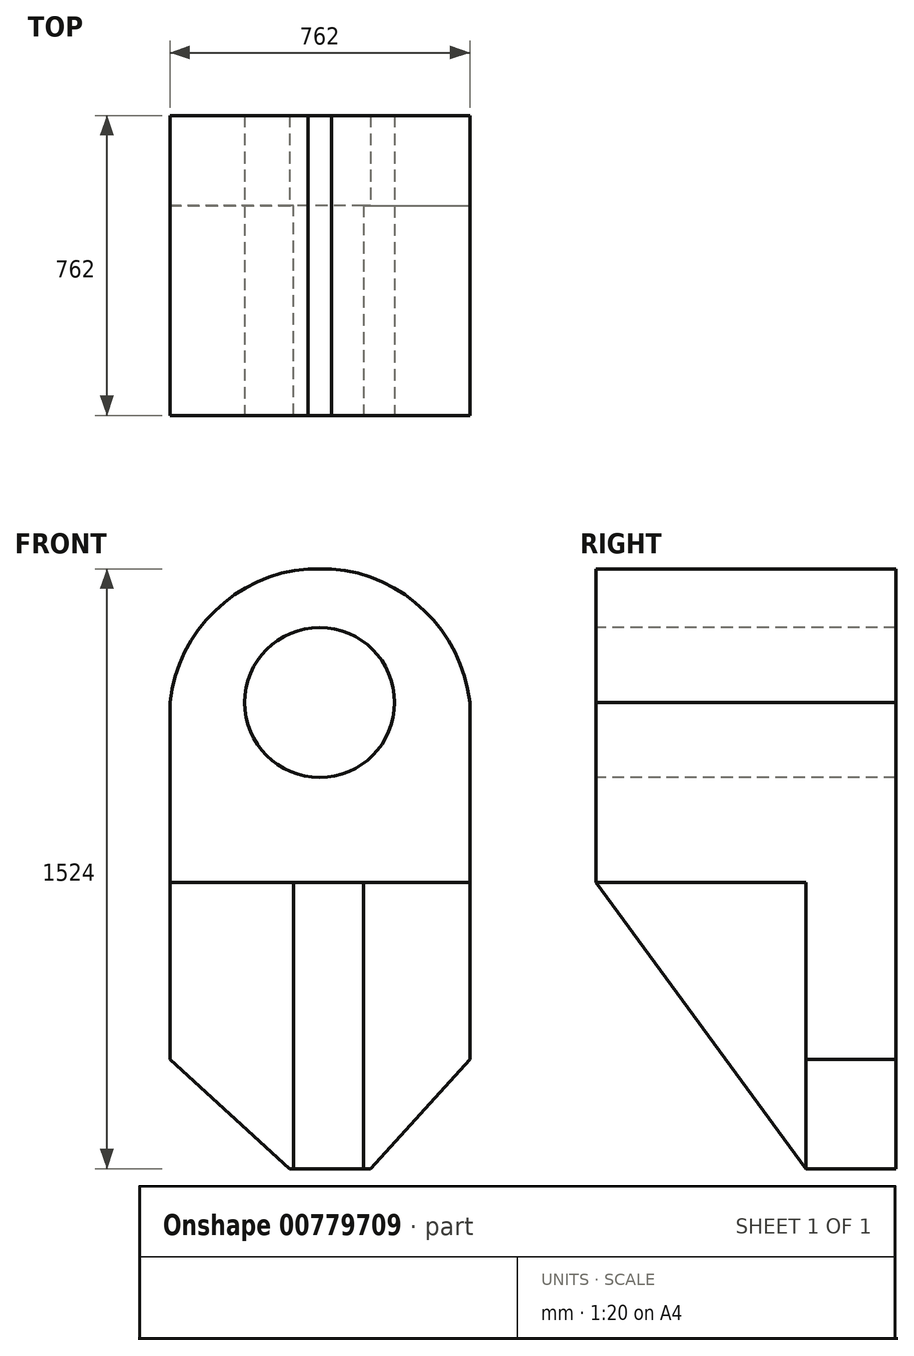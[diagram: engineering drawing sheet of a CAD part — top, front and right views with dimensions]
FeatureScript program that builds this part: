
annotation { "Feature Type Name" : "Feature", "Feature Type Description" : "" }
export const myFeature = defineFeature(function(context is Context, id is Id, definition is map)
    precondition{}
    {
        {
            var Q0;
            Q0=qCreatedBy(makeId("Front.planeOp"),FACE);
            var sketch = newSketch(context, id + "F0", { "sketchPlane" : qUnion([Q0])});
            skLineSegment(sketch, "E0", {"start": v(0, 0) * mm, "end": v(762, 0) * mm});
            skLineSegment(sketch, "E1", {"start": v(762, 0) * mm, "end": v(762, -1524) * mm});
            skLineSegment(sketch, "E2", {"start": v(762, -1524) * mm, "end": v(0, -1524) * mm});
            skLineSegment(sketch, "E3", {"start": v(0, -1524) * mm, "end": v(0, 0) * mm});
            skSolve(sketch);
        }
        {
            var Q0;
            Q0 = qSketchRegion(id + "F0", true);
            extrude(context, id + "F1", {"entities" : qUnion([Q0]), "depth" : 762 * mm, "offsetDistance" : 25.4 * mm});
        }
        {
            var Q0;
            Q0=makeQuery(id+"F1.opExtrude","CAP_FACE",FACE,{"disambiguationData":[OSD([sQuery(id+"F0.wireOp",EDGE,"E0"),sQuery(id+"F0.wireOp",EDGE,"E1"),sQuery(id+"F0.wireOp",EDGE,"E2"),sQuery(id+"F0.wireOp",EDGE,"E3")])],"isStart":false});
            var sketch = newSketch(context, id + "F2", { "sketchPlane" : qUnion([Q0])});
            skLineSegment(sketch, "E4", {"start": v(0, -1524) * mm, "end": v(0, -457.2) * mm});
            skLineSegment(sketch, "E5", {"start": v(0, -457.2) * mm, "end": v(0, 0) * mm});
            skCircle(sketch, "E6", {"center": v(380.43, -339.55) * mm, "radius": 190.5 * mm});
            skLineSegment(sketch, "E7", {"start": v(380.43, -339.55) * mm, "end": v(762, -339.55) * mm});
            skLineSegment(sketch, "E8", {"start": v(380.43, -339.55) * mm, "end": v(0, -339.55) * mm});
            skLineSegment(sketch, "E9", {"start": v(0, -339.55) * mm, "end": v(0, -629.99) * mm});
            skLineSegment(sketch, "E10", {"start": v(0, -339.55) * mm, "end": v(0, -796.75) * mm});
            skLineSegment(sketch, "E11", {"start": v(762, -339.55) * mm, "end": v(762, -796.75) * mm});
            skArc(sketch, "E12", {"start": v(762, -339.55) * mm, "mid": v(381, 1.16) * mm, "end": v(0, -339.55) * mm});
            skLineSegment(sketch, "E13", {"start": v(314.58, -796.75) * mm, "end": v(314.58, -1524) * mm});
            skLineSegment(sketch, "E14", {"start": v(492.38, -796.75) * mm, "end": v(492.38, -1524) * mm});
            skLineSegment(sketch, "E15", {"start": v(0, -796.75) * mm, "end": v(314.58, -796.75) * mm});
            skLineSegment(sketch, "E16", {"start": v(492.38, -796.75) * mm, "end": v(762, -796.75) * mm});
            skLineSegment(sketch, "E17", {"start": v(0, -1524) * mm, "end": v(228.6, -1524) * mm});
            skLineSegment(sketch, "E18", {"start": v(533.4, -1524) * mm, "end": v(762, -1524) * mm});
            skLineSegment(sketch, "E19", {"start": v(228.6, -1524) * mm, "end": v(533.4, -1524) * mm});
            skLineSegment(sketch, "E20", {"start": v(762, -1524) * mm, "end": v(762, -1382.54) * mm});
            skSolve(sketch);
        }
        {
            var Q0;
            Q0=makeQuery(id+"F1.opExtrude","CAP_FACE",FACE,{"disambiguationData":[OSD([sQuery(id+"F0.wireOp",EDGE,"E0"),sQuery(id+"F0.wireOp",EDGE,"E1"),sQuery(id+"F0.wireOp",EDGE,"E2"),sQuery(id+"F0.wireOp",EDGE,"E3")])],"isStart":false});
            var sketch = newSketch(context, id + "F3", { "sketchPlane" : qUnion([Q0])});
            skLineSegment(sketch, "E21", {"start": v(0, -1246.67) * mm, "end": v(304.57, -1524) * mm});
            skLineSegment(sketch, "E22", {"start": v(762, -1246.67) * mm, "end": v(509.47, -1524) * mm});
            skSolve(sketch);
        }
        {
            var Q0;
            {var subQ0=sQuery(id+"F3.wireOp",EDGE,"E22");Q0=makeQuery(id+"F3.imprint","IMPRINT",FACE,{"disambiguationData":[TD([[makeQuery(id+"F3.imprint","IMPRINT",EDGE,{"derivedFrom":subQ0}),1.0]])]});}
            var Q1;
            {var subQ0=sQuery(id+"F3.wireOp",EDGE,"E21");Q1=makeQuery(id+"F3.imprint","IMPRINT",FACE,{"disambiguationData":[TD([[makeQuery(id+"F3.imprint","IMPRINT",EDGE,{"derivedFrom":subQ0}),-1.0]])]});}
            var Q2;
            {var subQ1=makeQuery(id+"F1.opExtrude","CAP_EDGE",EDGE,{"disambiguationData":[OSD([sQuery(id+"F0.wireOp",EDGE,"E1")])],"isStart":false});var subQ3=makeQuery(id+"F1.opExtrude","CAP_EDGE",EDGE,{"disambiguationData":[OSD([sQuery(id+"F0.wireOp",EDGE,"E0")])],"isStart":false});var subQ5=makeQuery(id+"F2.imprint","INTERSECT",VERTEX,{"derivedFrom":[subQ3,subQ1]});Q2=makeQuery(id+"F2.imprint","IMPRINT",FACE,{"disambiguationData":[TD([[makeQuery(id+"F2.imprint","IMPRINT",EDGE,{"disambiguationData":[TD([[subQ5,1.0]])],"derivedFrom":subQ3}),-1.0]])]});}
            var Q3;
            {var subQ0=sQuery(id+"F2.wireOp",EDGE,"E5");Q3=makeQuery(id+"F2.imprint","IMPRINT",FACE,{"disambiguationData":[TD([[makeQuery(id+"F2.imprint","IMPRINT",EDGE,{"derivedFrom":subQ0}),-1.0]])]});}
            extrude(context, id + "F4", {"entities" : qUnion([Q0, Q1, Q2, Q3]), "operationType" : NewBodyOperationType.REMOVE, "endBound" : BoundingType.THROUGH_ALL, "oppositeDirection" : true, "depth" : 25.4 * mm, "offsetDistance" : 25.4 * mm});
        }
        {
            var Q0;
            {var subQ0=sQuery(id+"F2.wireOp",EDGE,"E7");var subQ1=sQuery(id+"F2.wireOp",EDGE,"E6");var subQ2=makeQuery(id+"F2.imprint","INTERSECT",VERTEX,{"derivedFrom":[subQ1,subQ0]});Q0=makeQuery(id+"F2.imprint","IMPRINT",FACE,{"disambiguationData":[TD([[makeQuery(id+"F2.imprint","IMPRINT",EDGE,{"disambiguationData":[TD([[subQ2,-1.0]])],"derivedFrom":subQ1}),1.0]])]});}
            var Q1;
            {var subQ0=sQuery(id+"F2.wireOp",EDGE,"E7");var subQ1=sQuery(id+"F2.wireOp",EDGE,"E6");var subQ2=makeQuery(id+"F2.imprint","INTERSECT",VERTEX,{"derivedFrom":[subQ1,subQ0]});Q1=makeQuery(id+"F2.imprint","IMPRINT",FACE,{"disambiguationData":[TD([[makeQuery(id+"F2.imprint","IMPRINT",EDGE,{"disambiguationData":[TD([[subQ2,1.0]])],"derivedFrom":subQ1}),1.0]])]});}
            extrude(context, id + "F5", {"entities" : qUnion([Q0, Q1]), "operationType" : NewBodyOperationType.REMOVE, "endBound" : BoundingType.THROUGH_ALL, "oppositeDirection" : true, "depth" : 25.4 * mm, "offsetDistance" : 25.4 * mm});
        }
        {
            var Q0;
            {var subQ5=sQuery(id+"F2.wireOp",EDGE,"E14");Q0=makeQuery(id+"F2.imprint","IMPRINT",FACE,{"disambiguationData":[TD([[makeQuery(id+"F2.imprint","IMPRINT",EDGE,{"derivedFrom":subQ5}),1.0]])]});}
            var Q1;
            Q1=makeQuery(id+"F2.imprint","IMPRINT",FACE,{"disambiguationData":[TD([[makeQuery(id+"F2.imprint","IMPRINT",EDGE,{"derivedFrom":sQuery(id+"F2.wireOp",EDGE,"E4")}),-1.0]])]});
            extrude(context, id + "F6", {"entities" : qUnion([Q0, Q1]), "operationType" : NewBodyOperationType.REMOVE, "oppositeDirection" : true, "depth" : 533.4 * mm, "offsetDistance" : 25.4 * mm});
        }
        {
            var Q0;
            Q0=makeQuery(id+"F6.boolean.opBoolean","COPY",FACE,{"derivedFrom":makeQuery(id+"F6.opExtrude","SWEPT_FACE",FACE,{"disambiguationData":[OSD([sQuery(id+"F2.wireOp",EDGE,"E13")])]})});
            var sketch = newSketch(context, id + "F7", { "sketchPlane" : qUnion([Q0])});
            skLineSegment(sketch, "E23", {"start": v(762, -796.75) * mm, "end": v(228.6, -1524) * mm});
            skSolve(sketch);
        }
        {
            var Q0;
            Q0 = qSketchRegion(id + "F7", true);
            var Q1;
            Q1=makeQuery(id+"F7.imprint","IMPRINT",FACE,{"disambiguationData":[TD([[makeQuery(id+"F7.imprint","IMPRINT",EDGE,{"derivedFrom":sQuery(id+"F7.wireOp",EDGE,"E23")}),1.0]])]});
            extrude(context, id + "F8", {"entities" : qUnion([Q0, Q1]), "operationType" : NewBodyOperationType.REMOVE, "endBound" : BoundingType.THROUGH_ALL, "oppositeDirection" : true, "depth" : 25.4 * mm, "offsetDistance" : 25.4 * mm});
        }
    });
